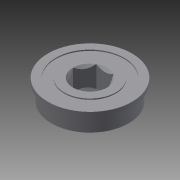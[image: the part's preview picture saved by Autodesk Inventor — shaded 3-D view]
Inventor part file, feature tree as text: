
AUTODESK INVENTOR PART (.ipt)
format: ipt  version: 2013 (Build 170138000, 138)  size: 160,768 bytes
history: native  units: in
note: dims shown in document units (in); Inventor stores cm internally (conversion verified against a paired STEP export)
features: sketch x4, extrude x2, hole x2, other x1, chamfer x1, imported_body x1
ambient origin geometry x8: Origin, YZ Plane, XZ Plane, XY Plane, X Axis, Y Axis, Z Axis, Center Point
feature tree (11):
  other  "Cut-Extrude1"
  extrude  "Extrusion1"  Depth=0.015in TaperAngle=0.0deg
  chamfer  "Chamfer1"  Distance=0.015in Angle=45.0deg
  extrude  "Extrusion2"  TaperAngle=0.0deg  [1 undecoded]
  hole  "Hole3"  [1 undecoded]
  hole  "Hole4"  [1 undecoded]
  imported_body  "Base1"
  sketch  "Sketch3"  dims[d14=0.75in d15=0.015in d16=0.0in d17=0.015in d18=0.125in d19=45.0deg]
  sketch  "Sketch4"  dims[d20=0.25in d21=0.0in]
  sketch  "Sketch5"  dims[d22=0.3125in d23=0.0in]
  sketch  "Sketch6"  dims[d24=0.25in d25=0.75in d26=0.5in d27=0.25in d28=0.5635in d29=1.0in d30=0.8108in d31=0.25in d32=0.75in d33=0.5in d34=0.25in d35=0.5635in d36=1.0in d37=0.8108in]
note: 3 required parameter values undecoded (feature->parameter linkage not recoverable at this tier; creation-order binding heuristic only, values carry confidence <= 0.55)
